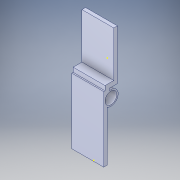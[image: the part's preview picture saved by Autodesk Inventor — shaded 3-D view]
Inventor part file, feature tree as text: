
AUTODESK INVENTOR PART (.ipt)
format: ipt  version: 2018 (Build 220112000, 112)  size: 157,696 bytes
history: native  units: in
note: dims shown in document units (in); Inventor stores cm internally (conversion verified against a paired STEP export)
features: sketch x6, extrude x4, other x1
ambient origin geometry x8: Origin, YZ Plane, XZ Plane, XY Plane, X Axis, Y Axis, Z Axis, Center Point
bodies: Solid1 (feature_tree)
feature tree (11):
  sketch  "Sketch1"  dims[d0=0.5906in d1=0.0in d2=0.3937in d3=0.0in]
  extrude  "Extrusion1"  Depth=0.3937in TaperAngle=0.0deg
  extrude  "Extrusion2"  Depth=0.4724in TaperAngle=0.0deg
  sketch  "Sketch4"
  extrude  "Extrusion3"  [1 undecoded]
  extrude  "Extrusion4"  [1 undecoded]
  sketch  "Sketch2"  dims[d4=0.9843in d5=0.0in d6=0.4724in d7=0.0in]
  sketch  "Sketch3"
  sketch  "Sketch5"
  sketch  "Sketch6"
  other  "Boss-Extrude7"
note: 2 required parameter values undecoded (feature->parameter linkage not recoverable at this tier; creation-order binding heuristic only, values carry confidence <= 0.55)
